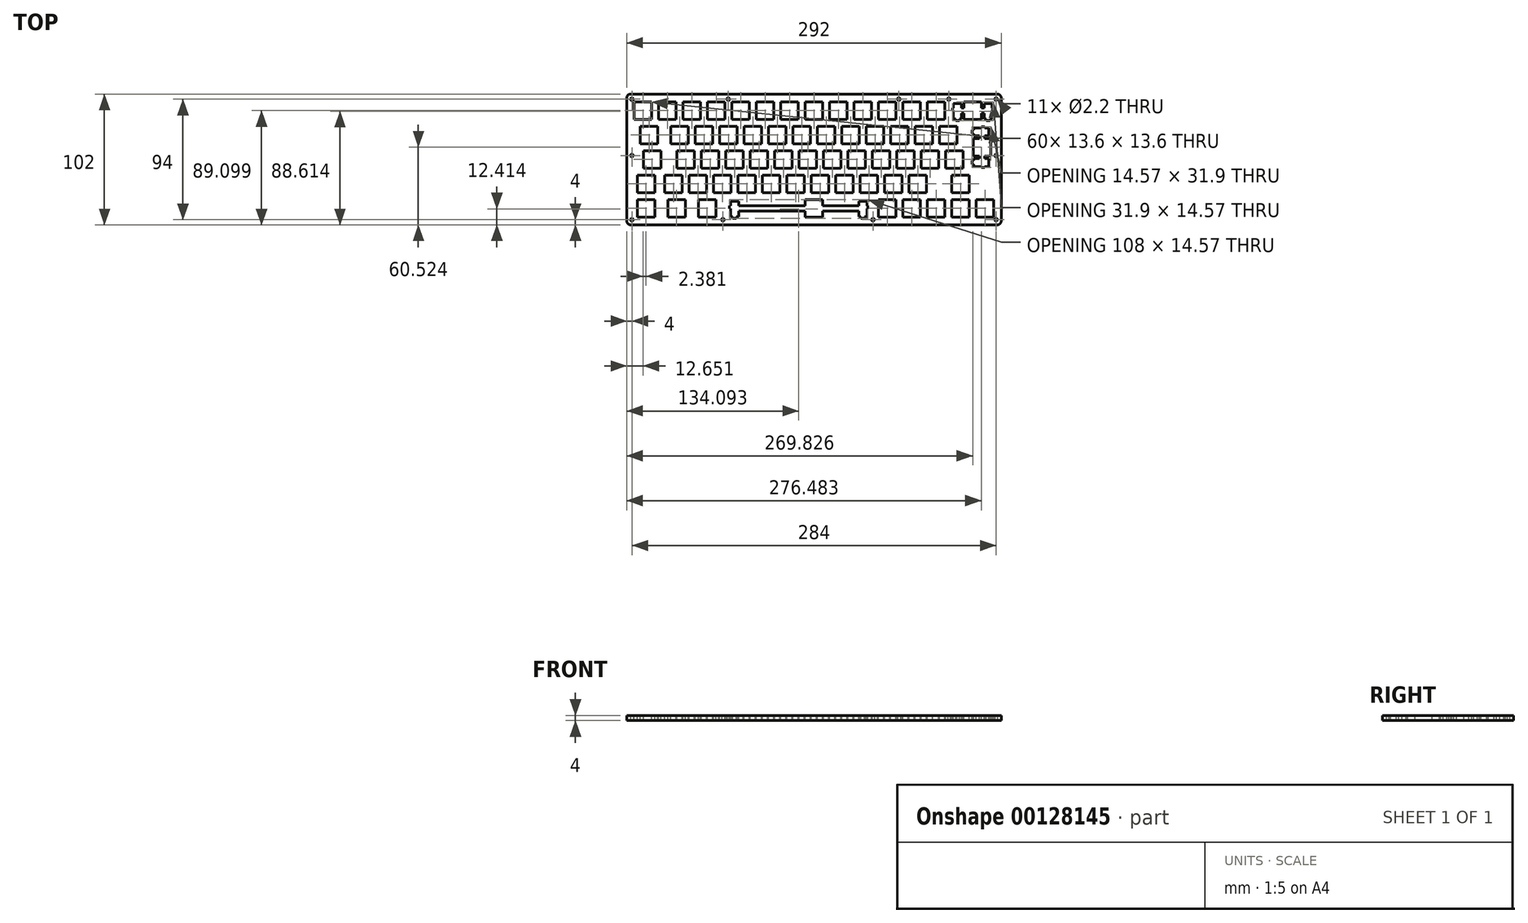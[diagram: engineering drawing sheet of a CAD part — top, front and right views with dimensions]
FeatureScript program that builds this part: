
annotation { "Feature Type Name" : "Feature", "Feature Type Description" : "" }
export const myFeature = defineFeature(function(context is Context, id is Id, definition is map)
    precondition{}
    {
        {
            var Q0;
            Q0=qCreatedBy(makeId("Top.planeOp"),FACE);
            var sketch = newSketch(context, id + "F0", { "sketchPlane" : qUnion([Q0])});
            skLineSegment(sketch, "E0.bottom", {"start": v(-143, 51) * mm, "end": v(143, 51) * mm});
            skLineSegment(sketch, "E0.top", {"start": v(-143, -51) * mm, "end": v(143, -51) * mm});
            skLineSegment(sketch, "E0.left", {"start": v(-146, 48) * mm, "end": v(-146, -48) * mm});
            skLineSegment(sketch, "E0.right", {"start": v(146, 48) * mm, "end": v(146, -48) * mm});
            skPoint(sketch, "E0.middle", {"position": v(0, 0) * mm});
            skPoint(sketch, "E1.visualSharp", {"position": v(-146, 51) * mm});
            skArc(sketch, "E1.filletArc", {"start": v(-143, 51) * mm, "mid": v(-145.12, 50.12) * mm, "end": v(-146, 48) * mm});
            skPoint(sketch, "E2.visualSharp", {"position": v(-146, -51) * mm});
            skArc(sketch, "E2.filletArc", {"start": v(-146, -48) * mm, "mid": v(-145.12, -50.12) * mm, "end": v(-143, -51) * mm});
            skPoint(sketch, "E3.visualSharp", {"position": v(146, 51) * mm});
            skArc(sketch, "E3.filletArc", {"start": v(146, 48) * mm, "mid": v(145.12, 50.12) * mm, "end": v(143, 51) * mm});
            skPoint(sketch, "E4.visualSharp", {"position": v(146, -51) * mm});
            skArc(sketch, "E4.filletArc", {"start": v(143, -51) * mm, "mid": v(145.12, -50.12) * mm, "end": v(146, -48) * mm});
            skCircle(sketch, "E5", {"center": v(-142, 47) * mm, "radius": 1.1 * mm});
            skCircle(sketch, "E6", {"center": v(-66.83, 47) * mm, "radius": 1.1 * mm});
            skCircle(sketch, "E7", {"center": v(66.17, 47) * mm, "radius": 1.1 * mm});
            skCircle(sketch, "E8", {"center": v(105.17, 47) * mm, "radius": 1.1 * mm});
            skCircle(sketch, "E9", {"center": v(142, 47) * mm, "radius": 1.1 * mm});
            skCircle(sketch, "E10", {"center": v(-142, -47) * mm, "radius": 1.1 * mm});
            skCircle(sketch, "E11", {"center": v(142, -47) * mm, "radius": 1.1 * mm});
            skCircle(sketch, "E12", {"center": v(-71, -47) * mm, "radius": 1.1 * mm});
            skCircle(sketch, "E13", {"center": v(46, -47) * mm, "radius": 1.1 * mm});
            skCircle(sketch, "E14", {"center": v(-142, 3) * mm, "radius": 1.1 * mm});
            skCircle(sketch, "E15", {"center": v(142, 3) * mm, "radius": 1.1 * mm});
            skSolve(sketch);
        }
        {
            var Q0;
            Q0 = qSketchRegion(id + "F0", true);
            extrude(context, id + "F1", {"entities" : qUnion([Q0]), "depth" : 4 * mm});
        }
        {
            var Q0;
            Q0=makeQuery(id+"F1.opExtrude","CAP_FACE",FACE,{"disambiguationData":[OSD([sQuery(id+"F0.wireOp",EDGE,"E0.bottom"),sQuery(id+"F0.wireOp",EDGE,"E0.top"),sQuery(id+"F0.wireOp",EDGE,"E0.left"),sQuery(id+"F0.wireOp",EDGE,"E0.right"),sQuery(id+"F0.wireOp",EDGE,"E1.filletArc"),sQuery(id+"F0.wireOp",EDGE,"E2.filletArc"),sQuery(id+"F0.wireOp",EDGE,"E3.filletArc"),sQuery(id+"F0.wireOp",EDGE,"E4.filletArc"),sQuery(id+"F0.wireOp",EDGE,"E5"),sQuery(id+"F0.wireOp",EDGE,"E6"),sQuery(id+"F0.wireOp",EDGE,"E7"),sQuery(id+"F0.wireOp",EDGE,"E8"),sQuery(id+"F0.wireOp",EDGE,"E9"),sQuery(id+"F0.wireOp",EDGE,"E10"),sQuery(id+"F0.wireOp",EDGE,"E11"),sQuery(id+"F0.wireOp",EDGE,"E12"),sQuery(id+"F0.wireOp",EDGE,"E13"),sQuery(id+"F0.wireOp",EDGE,"E14"),sQuery(id+"F0.wireOp",EDGE,"E15")])],"isStart":false});
            var sketch = newSketch(context, id + "F2", { "sketchPlane" : qUnion([Q0])});
            skLineSegment(sketch, "E16", {"start": v(-58.78, -36) * mm, "end": v(-58.78, -32.77) * mm});
            skLineSegment(sketch, "E17", {"start": v(-58.78, -32.77) * mm, "end": v(-65.03, -32.77) * mm});
            skLineSegment(sketch, "E18", {"start": v(-65.03, -32.77) * mm, "end": v(-65.03, -36) * mm});
            skLineSegment(sketch, "E19", {"start": v(-65.03, -36) * mm, "end": v(-65.9, -36) * mm});
            skLineSegment(sketch, "E20", {"start": v(-65.9, -36) * mm, "end": v(-65.9, -38.4) * mm});
            skLineSegment(sketch, "E21", {"start": v(-65.9, -38.4) * mm, "end": v(-65.03, -38.4) * mm});
            skLineSegment(sketch, "E22", {"start": v(-65.03, -38.4) * mm, "end": v(-65.03, -44.67) * mm});
            skLineSegment(sketch, "E23", {"start": v(-65.03, -44.67) * mm, "end": v(-63.36, -44.67) * mm});
            skLineSegment(sketch, "E24", {"start": v(-63.36, -44.67) * mm, "end": v(-63.36, -45.87) * mm});
            skLineSegment(sketch, "E25", {"start": v(-63.36, -45.87) * mm, "end": v(-60.46, -45.87) * mm});
            skLineSegment(sketch, "E26", {"start": v(-60.46, -45.87) * mm, "end": v(-60.46, -44.67) * mm});
            skLineSegment(sketch, "E27", {"start": v(-60.46, -44.67) * mm, "end": v(-58.78, -44.67) * mm});
            skLineSegment(sketch, "E28", {"start": v(-58.78, -44.67) * mm, "end": v(-58.78, -40.2) * mm});
            skLineSegment(sketch, "E29", {"start": v(-6.8, -44.9) * mm, "end": v(-6.8, -40.2) * mm});
            skLineSegment(sketch, "E30", {"start": v(6.8, -40.2) * mm, "end": v(34.97, -40.2) * mm});
            skLineSegment(sketch, "E31", {"start": v(34.97, -40.2) * mm, "end": v(34.97, -44.67) * mm});
            skLineSegment(sketch, "E32", {"start": v(34.97, -44.67) * mm, "end": v(36.64, -44.67) * mm});
            skLineSegment(sketch, "E33", {"start": v(36.64, -44.67) * mm, "end": v(36.64, -45.87) * mm});
            skLineSegment(sketch, "E34", {"start": v(36.64, -45.87) * mm, "end": v(39.54, -45.87) * mm});
            skLineSegment(sketch, "E35", {"start": v(39.54, -45.87) * mm, "end": v(39.54, -44.67) * mm});
            skLineSegment(sketch, "E36", {"start": v(39.54, -44.67) * mm, "end": v(41.22, -44.67) * mm});
            skLineSegment(sketch, "E37", {"start": v(41.22, -44.67) * mm, "end": v(41.22, -38.4) * mm});
            skLineSegment(sketch, "E38", {"start": v(41.22, -38.4) * mm, "end": v(42.1, -38.4) * mm});
            skLineSegment(sketch, "E39", {"start": v(42.1, -38.4) * mm, "end": v(42.1, -36) * mm});
            skLineSegment(sketch, "E40", {"start": v(42.1, -36) * mm, "end": v(41.22, -36) * mm});
            skLineSegment(sketch, "E41", {"start": v(41.22, -36) * mm, "end": v(41.22, -32.77) * mm});
            skLineSegment(sketch, "E42", {"start": v(41.22, -32.77) * mm, "end": v(34.97, -32.77) * mm});
            skLineSegment(sketch, "E43", {"start": v(34.97, -32.77) * mm, "end": v(34.97, -36) * mm});
            skLineSegment(sketch, "E44", {"start": v(34.97, -36) * mm, "end": v(6.8, -36) * mm});
            skLineSegment(sketch, "E45", {"start": v(-137.77, -31.3) * mm, "end": v(-124.17, -31.3) * mm});
            skLineSegment(sketch, "E46", {"start": v(-124.17, -31.3) * mm, "end": v(-124.17, -44.9) * mm});
            skLineSegment(sketch, "E47", {"start": v(-124.17, -44.9) * mm, "end": v(-137.77, -44.9) * mm});
            skLineSegment(sketch, "E48", {"start": v(-137.77, -44.9) * mm, "end": v(-137.77, -31.3) * mm});
            skLineSegment(sketch, "E49", {"start": v(-113.96, -31.3) * mm, "end": v(-100.36, -31.3) * mm});
            skLineSegment(sketch, "E50", {"start": v(-100.36, -31.3) * mm, "end": v(-100.36, -44.9) * mm});
            skLineSegment(sketch, "E51", {"start": v(-100.36, -44.9) * mm, "end": v(-113.96, -44.9) * mm});
            skLineSegment(sketch, "E52", {"start": v(-113.96, -44.9) * mm, "end": v(-113.96, -31.3) * mm});
            skLineSegment(sketch, "E53", {"start": v(-90.14, -31.3) * mm, "end": v(-76.54, -31.3) * mm});
            skLineSegment(sketch, "E54", {"start": v(-76.54, -31.3) * mm, "end": v(-76.54, -44.9) * mm});
            skLineSegment(sketch, "E55", {"start": v(-76.54, -44.9) * mm, "end": v(-90.14, -44.9) * mm});
            skLineSegment(sketch, "E56", {"start": v(-90.14, -44.9) * mm, "end": v(-90.14, -31.3) * mm});
            skLineSegment(sketch, "E57", {"start": v(50.35, -31.3) * mm, "end": v(63.95, -31.3) * mm});
            skLineSegment(sketch, "E58", {"start": v(63.95, -31.3) * mm, "end": v(63.95, -44.9) * mm});
            skLineSegment(sketch, "E59", {"start": v(63.95, -44.9) * mm, "end": v(50.35, -44.9) * mm});
            skLineSegment(sketch, "E60", {"start": v(50.35, -44.9) * mm, "end": v(50.35, -31.3) * mm});
            skLineSegment(sketch, "E61", {"start": v(69.4, -31.3) * mm, "end": v(83, -31.3) * mm});
            skLineSegment(sketch, "E62", {"start": v(83, -31.3) * mm, "end": v(83, -44.9) * mm});
            skLineSegment(sketch, "E63", {"start": v(83, -44.9) * mm, "end": v(69.4, -44.9) * mm});
            skLineSegment(sketch, "E64", {"start": v(69.4, -44.9) * mm, "end": v(69.4, -31.3) * mm});
            skLineSegment(sketch, "E65", {"start": v(88.45, -31.3) * mm, "end": v(102.05, -31.3) * mm});
            skLineSegment(sketch, "E66", {"start": v(102.05, -31.3) * mm, "end": v(102.05, -44.9) * mm});
            skLineSegment(sketch, "E67", {"start": v(102.05, -44.9) * mm, "end": v(88.45, -44.9) * mm});
            skLineSegment(sketch, "E68", {"start": v(88.45, -44.9) * mm, "end": v(88.45, -31.3) * mm});
            skLineSegment(sketch, "E69", {"start": v(107.5, -31.3) * mm, "end": v(121.1, -31.3) * mm});
            skLineSegment(sketch, "E70", {"start": v(121.1, -31.3) * mm, "end": v(121.1, -44.9) * mm});
            skLineSegment(sketch, "E71", {"start": v(121.1, -44.9) * mm, "end": v(107.5, -44.9) * mm});
            skLineSegment(sketch, "E72", {"start": v(107.5, -44.9) * mm, "end": v(107.5, -31.3) * mm});
            skLineSegment(sketch, "E73", {"start": v(126.55, -31.3) * mm, "end": v(140.15, -31.3) * mm});
            skLineSegment(sketch, "E74", {"start": v(140.15, -31.3) * mm, "end": v(140.15, -44.9) * mm});
            skLineSegment(sketch, "E75", {"start": v(140.15, -44.9) * mm, "end": v(126.55, -44.9) * mm});
            skLineSegment(sketch, "E76", {"start": v(126.55, -44.9) * mm, "end": v(126.55, -31.3) * mm});
            skLineSegment(sketch, "E77", {"start": v(-137.77, -12.25) * mm, "end": v(-124.17, -12.25) * mm});
            skLineSegment(sketch, "E78", {"start": v(-124.17, -12.25) * mm, "end": v(-124.17, -25.85) * mm});
            skLineSegment(sketch, "E79", {"start": v(-124.17, -25.85) * mm, "end": v(-137.77, -25.85) * mm});
            skLineSegment(sketch, "E80", {"start": v(-137.77, -25.85) * mm, "end": v(-137.77, -12.25) * mm});
            skLineSegment(sketch, "E81", {"start": v(-116.34, -12.25) * mm, "end": v(-102.74, -12.25) * mm});
            skLineSegment(sketch, "E82", {"start": v(-102.74, -12.25) * mm, "end": v(-102.74, -25.85) * mm});
            skLineSegment(sketch, "E83", {"start": v(-102.74, -25.85) * mm, "end": v(-116.34, -25.85) * mm});
            skLineSegment(sketch, "E84", {"start": v(-116.34, -25.85) * mm, "end": v(-116.34, -12.25) * mm});
            skLineSegment(sketch, "E85", {"start": v(-97.29, -12.25) * mm, "end": v(-83.69, -12.25) * mm});
            skLineSegment(sketch, "E86", {"start": v(-83.69, -12.25) * mm, "end": v(-83.69, -25.85) * mm});
            skLineSegment(sketch, "E87", {"start": v(-83.69, -25.85) * mm, "end": v(-97.29, -25.85) * mm});
            skLineSegment(sketch, "E88", {"start": v(-97.29, -25.85) * mm, "end": v(-97.29, -12.25) * mm});
            skLineSegment(sketch, "E89", {"start": v(-78.24, -12.25) * mm, "end": v(-64.64, -12.25) * mm});
            skLineSegment(sketch, "E90", {"start": v(-64.64, -12.25) * mm, "end": v(-64.64, -25.85) * mm});
            skLineSegment(sketch, "E91", {"start": v(-64.64, -25.85) * mm, "end": v(-78.24, -25.85) * mm});
            skLineSegment(sketch, "E92", {"start": v(-78.24, -25.85) * mm, "end": v(-78.24, -12.25) * mm});
            skLineSegment(sketch, "E93", {"start": v(-59.19, -12.25) * mm, "end": v(-45.59, -12.25) * mm});
            skLineSegment(sketch, "E94", {"start": v(-45.59, -12.25) * mm, "end": v(-45.59, -25.85) * mm});
            skLineSegment(sketch, "E95", {"start": v(-45.59, -25.85) * mm, "end": v(-59.19, -25.85) * mm});
            skLineSegment(sketch, "E96", {"start": v(-59.19, -25.85) * mm, "end": v(-59.19, -12.25) * mm});
            skLineSegment(sketch, "E97", {"start": v(-40.14, -12.25) * mm, "end": v(-26.54, -12.25) * mm});
            skLineSegment(sketch, "E98", {"start": v(-26.54, -12.25) * mm, "end": v(-26.54, -25.85) * mm});
            skLineSegment(sketch, "E99", {"start": v(-26.54, -25.85) * mm, "end": v(-40.14, -25.85) * mm});
            skLineSegment(sketch, "E100", {"start": v(-40.14, -25.85) * mm, "end": v(-40.14, -12.25) * mm});
            skLineSegment(sketch, "E101", {"start": v(-21.09, -12.25) * mm, "end": v(-7.49, -12.25) * mm});
            skLineSegment(sketch, "E102", {"start": v(-7.49, -12.25) * mm, "end": v(-7.49, -25.85) * mm});
            skLineSegment(sketch, "E103", {"start": v(-7.49, -25.85) * mm, "end": v(-21.09, -25.85) * mm});
            skLineSegment(sketch, "E104", {"start": v(-21.09, -25.85) * mm, "end": v(-21.09, -12.25) * mm});
            skLineSegment(sketch, "E105", {"start": v(-2.04, -12.25) * mm, "end": v(11.56, -12.25) * mm});
            skLineSegment(sketch, "E106", {"start": v(11.56, -12.25) * mm, "end": v(11.56, -25.85) * mm});
            skLineSegment(sketch, "E107", {"start": v(11.56, -25.85) * mm, "end": v(-2.04, -25.85) * mm});
            skLineSegment(sketch, "E108", {"start": v(-2.04, -25.85) * mm, "end": v(-2.04, -12.25) * mm});
            skLineSegment(sketch, "E109", {"start": v(17.01, -12.25) * mm, "end": v(30.61, -12.25) * mm});
            skLineSegment(sketch, "E110", {"start": v(30.61, -12.25) * mm, "end": v(30.61, -25.85) * mm});
            skLineSegment(sketch, "E111", {"start": v(30.61, -25.85) * mm, "end": v(17.01, -25.85) * mm});
            skLineSegment(sketch, "E112", {"start": v(17.01, -25.85) * mm, "end": v(17.01, -12.25) * mm});
            skLineSegment(sketch, "E113", {"start": v(36.06, -12.25) * mm, "end": v(49.66, -12.25) * mm});
            skLineSegment(sketch, "E114", {"start": v(49.66, -12.25) * mm, "end": v(49.66, -25.85) * mm});
            skLineSegment(sketch, "E115", {"start": v(49.66, -25.85) * mm, "end": v(36.06, -25.85) * mm});
            skLineSegment(sketch, "E116", {"start": v(36.06, -25.85) * mm, "end": v(36.06, -12.25) * mm});
            skLineSegment(sketch, "E117", {"start": v(55.11, -12.25) * mm, "end": v(68.71, -12.25) * mm});
            skLineSegment(sketch, "E118", {"start": v(68.71, -12.25) * mm, "end": v(68.71, -25.85) * mm});
            skLineSegment(sketch, "E119", {"start": v(68.71, -25.85) * mm, "end": v(55.11, -25.85) * mm});
            skLineSegment(sketch, "E120", {"start": v(55.11, -25.85) * mm, "end": v(55.11, -12.25) * mm});
            skLineSegment(sketch, "E121", {"start": v(74.16, -12.25) * mm, "end": v(87.76, -12.25) * mm});
            skLineSegment(sketch, "E122", {"start": v(87.76, -12.25) * mm, "end": v(87.76, -25.85) * mm});
            skLineSegment(sketch, "E123", {"start": v(87.76, -25.85) * mm, "end": v(74.16, -25.85) * mm});
            skLineSegment(sketch, "E124", {"start": v(74.16, -25.85) * mm, "end": v(74.16, -12.25) * mm});
            skLineSegment(sketch, "E125", {"start": v(107.5, -12.25) * mm, "end": v(121.1, -12.25) * mm});
            skLineSegment(sketch, "E126", {"start": v(121.1, -12.25) * mm, "end": v(121.1, -25.85) * mm});
            skLineSegment(sketch, "E127", {"start": v(121.1, -25.85) * mm, "end": v(107.5, -25.85) * mm});
            skLineSegment(sketch, "E128", {"start": v(107.5, -25.85) * mm, "end": v(107.5, -12.25) * mm});
            skLineSegment(sketch, "E129", {"start": v(-133, 6.8) * mm, "end": v(-119.4, 6.8) * mm});
            skLineSegment(sketch, "E130", {"start": v(-119.4, 6.8) * mm, "end": v(-119.4, -6.8) * mm});
            skLineSegment(sketch, "E131", {"start": v(-119.4, -6.8) * mm, "end": v(-133, -6.8) * mm});
            skLineSegment(sketch, "E132", {"start": v(-133, -6.8) * mm, "end": v(-133, 6.8) * mm});
            skLineSegment(sketch, "E133", {"start": v(-106.81, 6.8) * mm, "end": v(-93.21, 6.8) * mm});
            skLineSegment(sketch, "E134", {"start": v(-93.21, 6.8) * mm, "end": v(-93.21, -6.8) * mm});
            skLineSegment(sketch, "E135", {"start": v(-93.21, -6.8) * mm, "end": v(-106.81, -6.8) * mm});
            skLineSegment(sketch, "E136", {"start": v(-106.81, -6.8) * mm, "end": v(-106.81, 6.8) * mm});
            skLineSegment(sketch, "E137", {"start": v(-87.76, 6.8) * mm, "end": v(-74.16, 6.8) * mm});
            skLineSegment(sketch, "E138", {"start": v(-74.16, 6.8) * mm, "end": v(-74.16, -6.8) * mm});
            skLineSegment(sketch, "E139", {"start": v(-74.16, -6.8) * mm, "end": v(-87.76, -6.8) * mm});
            skLineSegment(sketch, "E140", {"start": v(-87.76, -6.8) * mm, "end": v(-87.76, 6.8) * mm});
            skLineSegment(sketch, "E141", {"start": v(-68.71, 6.8) * mm, "end": v(-55.11, 6.8) * mm});
            skLineSegment(sketch, "E142", {"start": v(-55.11, 6.8) * mm, "end": v(-55.11, -6.8) * mm});
            skLineSegment(sketch, "E143", {"start": v(-55.11, -6.8) * mm, "end": v(-68.71, -6.8) * mm});
            skLineSegment(sketch, "E144", {"start": v(-68.71, -6.8) * mm, "end": v(-68.71, 6.8) * mm});
            skLineSegment(sketch, "E145", {"start": v(-49.66, 6.8) * mm, "end": v(-36.06, 6.8) * mm});
            skLineSegment(sketch, "E146", {"start": v(-36.06, 6.8) * mm, "end": v(-36.06, -6.8) * mm});
            skLineSegment(sketch, "E147", {"start": v(-36.06, -6.8) * mm, "end": v(-49.66, -6.8) * mm});
            skLineSegment(sketch, "E148", {"start": v(-49.66, -6.8) * mm, "end": v(-49.66, 6.8) * mm});
            skLineSegment(sketch, "E149", {"start": v(-30.61, 6.8) * mm, "end": v(-17.01, 6.8) * mm});
            skLineSegment(sketch, "E150", {"start": v(-17.01, 6.8) * mm, "end": v(-17.01, -6.8) * mm});
            skLineSegment(sketch, "E151", {"start": v(-17.01, -6.8) * mm, "end": v(-30.61, -6.8) * mm});
            skLineSegment(sketch, "E152", {"start": v(-30.61, -6.8) * mm, "end": v(-30.61, 6.8) * mm});
            skLineSegment(sketch, "E153", {"start": v(-11.56, 6.8) * mm, "end": v(2.04, 6.8) * mm});
            skLineSegment(sketch, "E154", {"start": v(2.04, 6.8) * mm, "end": v(2.04, -6.8) * mm});
            skLineSegment(sketch, "E155", {"start": v(2.04, -6.8) * mm, "end": v(-11.56, -6.8) * mm});
            skLineSegment(sketch, "E156", {"start": v(-11.56, -6.8) * mm, "end": v(-11.56, 6.8) * mm});
            skLineSegment(sketch, "E157", {"start": v(7.49, 6.8) * mm, "end": v(21.09, 6.8) * mm});
            skLineSegment(sketch, "E158", {"start": v(21.09, 6.8) * mm, "end": v(21.09, -6.8) * mm});
            skLineSegment(sketch, "E159", {"start": v(21.09, -6.8) * mm, "end": v(7.49, -6.8) * mm});
            skLineSegment(sketch, "E160", {"start": v(7.49, -6.8) * mm, "end": v(7.49, 6.8) * mm});
            skLineSegment(sketch, "E161", {"start": v(26.54, 6.8) * mm, "end": v(40.14, 6.8) * mm});
            skLineSegment(sketch, "E162", {"start": v(40.14, 6.8) * mm, "end": v(40.14, -6.8) * mm});
            skLineSegment(sketch, "E163", {"start": v(40.14, -6.8) * mm, "end": v(26.54, -6.8) * mm});
            skLineSegment(sketch, "E164", {"start": v(26.54, -6.8) * mm, "end": v(26.54, 6.8) * mm});
            skLineSegment(sketch, "E165", {"start": v(45.59, 6.8) * mm, "end": v(59.19, 6.8) * mm});
            skLineSegment(sketch, "E166", {"start": v(59.19, 6.8) * mm, "end": v(59.19, -6.8) * mm});
            skLineSegment(sketch, "E167", {"start": v(59.19, -6.8) * mm, "end": v(45.59, -6.8) * mm});
            skLineSegment(sketch, "E168", {"start": v(45.59, -6.8) * mm, "end": v(45.59, 6.8) * mm});
            skLineSegment(sketch, "E169", {"start": v(64.64, 6.8) * mm, "end": v(78.24, 6.8) * mm});
            skLineSegment(sketch, "E170", {"start": v(78.24, 6.8) * mm, "end": v(78.24, -6.8) * mm});
            skLineSegment(sketch, "E171", {"start": v(78.24, -6.8) * mm, "end": v(64.64, -6.8) * mm});
            skLineSegment(sketch, "E172", {"start": v(64.64, -6.8) * mm, "end": v(64.64, 6.8) * mm});
            skLineSegment(sketch, "E173", {"start": v(83.69, 6.8) * mm, "end": v(97.29, 6.8) * mm});
            skLineSegment(sketch, "E174", {"start": v(97.29, 6.8) * mm, "end": v(97.29, -6.8) * mm});
            skLineSegment(sketch, "E175", {"start": v(97.29, -6.8) * mm, "end": v(83.69, -6.8) * mm});
            skLineSegment(sketch, "E176", {"start": v(83.69, -6.8) * mm, "end": v(83.69, 6.8) * mm});
            skLineSegment(sketch, "E177", {"start": v(102.74, 6.8) * mm, "end": v(116.34, 6.8) * mm});
            skLineSegment(sketch, "E178", {"start": v(116.34, 6.8) * mm, "end": v(116.34, -6.8) * mm});
            skLineSegment(sketch, "E179", {"start": v(116.34, -6.8) * mm, "end": v(102.74, -6.8) * mm});
            skLineSegment(sketch, "E180", {"start": v(102.74, -6.8) * mm, "end": v(102.74, 6.8) * mm});
            skLineSegment(sketch, "E181", {"start": v(130.67, 25.47) * mm, "end": v(130.67, 24.6) * mm});
            skLineSegment(sketch, "E182", {"start": v(130.67, 24.6) * mm, "end": v(124.4, 24.6) * mm});
            skLineSegment(sketch, "E183", {"start": v(124.4, 24.6) * mm, "end": v(124.4, 22.93) * mm});
            skLineSegment(sketch, "E184", {"start": v(124.4, 22.93) * mm, "end": v(123.2, 22.93) * mm});
            skLineSegment(sketch, "E185", {"start": v(123.2, 22.93) * mm, "end": v(123.2, 20.02) * mm});
            skLineSegment(sketch, "E186", {"start": v(123.2, 20.02) * mm, "end": v(124.4, 20.02) * mm});
            skLineSegment(sketch, "E187", {"start": v(124.4, 20.02) * mm, "end": v(124.4, 18.35) * mm});
            skLineSegment(sketch, "E188", {"start": v(124.4, 18.35) * mm, "end": v(128.87, 18.35) * mm});
            skLineSegment(sketch, "E189", {"start": v(128.87, 18.35) * mm, "end": v(128.87, 16.32) * mm});
            skLineSegment(sketch, "E190", {"start": v(128.87, 16.32) * mm, "end": v(124.17, 16.32) * mm});
            skLineSegment(sketch, "E191", {"start": v(124.17, 16.32) * mm, "end": v(124.17, 2.72) * mm});
            skLineSegment(sketch, "E192", {"start": v(124.17, 2.72) * mm, "end": v(128.87, 2.72) * mm});
            skLineSegment(sketch, "E193", {"start": v(128.87, 2.72) * mm, "end": v(128.87, 0.7) * mm});
            skLineSegment(sketch, "E194", {"start": v(128.87, 0.7) * mm, "end": v(124.4, 0.7) * mm});
            skLineSegment(sketch, "E195", {"start": v(124.4, 0.7) * mm, "end": v(124.4, -0.98) * mm});
            skLineSegment(sketch, "E196", {"start": v(124.4, -0.98) * mm, "end": v(123.2, -0.98) * mm});
            skLineSegment(sketch, "E197", {"start": v(123.2, -0.98) * mm, "end": v(123.2, -3.88) * mm});
            skLineSegment(sketch, "E198", {"start": v(123.2, -3.88) * mm, "end": v(124.4, -3.88) * mm});
            skLineSegment(sketch, "E199", {"start": v(124.4, -3.88) * mm, "end": v(124.4, -5.55) * mm});
            skLineSegment(sketch, "E200", {"start": v(124.4, -5.55) * mm, "end": v(130.67, -5.55) * mm});
            skLineSegment(sketch, "E201", {"start": v(130.67, -5.55) * mm, "end": v(130.67, -6.43) * mm});
            skLineSegment(sketch, "E202", {"start": v(130.67, -6.43) * mm, "end": v(133.07, -6.43) * mm});
            skLineSegment(sketch, "E203", {"start": v(133.07, -6.43) * mm, "end": v(133.07, -5.55) * mm});
            skLineSegment(sketch, "E204", {"start": v(133.07, -5.55) * mm, "end": v(136.3, -5.55) * mm});
            skLineSegment(sketch, "E205", {"start": v(136.3, -5.55) * mm, "end": v(136.3, 0.7) * mm});
            skLineSegment(sketch, "E206", {"start": v(136.3, 0.7) * mm, "end": v(133.07, 0.7) * mm});
            skLineSegment(sketch, "E207", {"start": v(133.07, 0.7) * mm, "end": v(133.07, 2.72) * mm});
            skLineSegment(sketch, "E208", {"start": v(133.07, 2.72) * mm, "end": v(137.77, 2.72) * mm});
            skLineSegment(sketch, "E209", {"start": v(137.77, 2.72) * mm, "end": v(137.77, 16.32) * mm});
            skLineSegment(sketch, "E210", {"start": v(137.77, 16.32) * mm, "end": v(133.07, 16.32) * mm});
            skLineSegment(sketch, "E211", {"start": v(133.07, 16.32) * mm, "end": v(133.07, 18.35) * mm});
            skLineSegment(sketch, "E212", {"start": v(133.07, 18.35) * mm, "end": v(136.3, 18.35) * mm});
            skLineSegment(sketch, "E213", {"start": v(136.3, 18.35) * mm, "end": v(136.3, 24.6) * mm});
            skLineSegment(sketch, "E214", {"start": v(136.3, 24.6) * mm, "end": v(133.07, 24.6) * mm});
            skLineSegment(sketch, "E215", {"start": v(133.07, 24.6) * mm, "end": v(133.07, 25.47) * mm});
            skLineSegment(sketch, "E216", {"start": v(133.07, 25.47) * mm, "end": v(130.67, 25.47) * mm});
            skLineSegment(sketch, "E217", {"start": v(-135.39, 25.85) * mm, "end": v(-121.79, 25.85) * mm});
            skLineSegment(sketch, "E218", {"start": v(-121.79, 25.85) * mm, "end": v(-121.79, 12.25) * mm});
            skLineSegment(sketch, "E219", {"start": v(-121.79, 12.25) * mm, "end": v(-135.39, 12.25) * mm});
            skLineSegment(sketch, "E220", {"start": v(-135.39, 12.25) * mm, "end": v(-135.39, 25.85) * mm});
            skLineSegment(sketch, "E221", {"start": v(-111.57, 25.85) * mm, "end": v(-97.98, 25.85) * mm});
            skLineSegment(sketch, "E222", {"start": v(-97.98, 25.85) * mm, "end": v(-97.98, 12.25) * mm});
            skLineSegment(sketch, "E223", {"start": v(-97.98, 12.25) * mm, "end": v(-111.57, 12.25) * mm});
            skLineSegment(sketch, "E224", {"start": v(-111.57, 12.25) * mm, "end": v(-111.57, 25.85) * mm});
            skLineSegment(sketch, "E225", {"start": v(-92.52, 25.85) * mm, "end": v(-78.93, 25.85) * mm});
            skLineSegment(sketch, "E226", {"start": v(-78.93, 25.85) * mm, "end": v(-78.93, 12.25) * mm});
            skLineSegment(sketch, "E227", {"start": v(-78.93, 12.25) * mm, "end": v(-92.52, 12.25) * mm});
            skLineSegment(sketch, "E228", {"start": v(-92.52, 12.25) * mm, "end": v(-92.52, 25.85) * mm});
            skLineSegment(sketch, "E229", {"start": v(-73.47, 25.85) * mm, "end": v(-59.88, 25.85) * mm});
            skLineSegment(sketch, "E230", {"start": v(-59.88, 25.85) * mm, "end": v(-59.88, 12.25) * mm});
            skLineSegment(sketch, "E231", {"start": v(-59.88, 12.25) * mm, "end": v(-73.47, 12.25) * mm});
            skLineSegment(sketch, "E232", {"start": v(-73.47, 12.25) * mm, "end": v(-73.47, 25.85) * mm});
            skLineSegment(sketch, "E233", {"start": v(-54.43, 25.85) * mm, "end": v(-40.83, 25.85) * mm});
            skLineSegment(sketch, "E234", {"start": v(-40.83, 25.85) * mm, "end": v(-40.83, 12.25) * mm});
            skLineSegment(sketch, "E235", {"start": v(-40.83, 12.25) * mm, "end": v(-54.43, 12.25) * mm});
            skLineSegment(sketch, "E236", {"start": v(-54.43, 12.25) * mm, "end": v(-54.43, 25.85) * mm});
            skLineSegment(sketch, "E237", {"start": v(-35.38, 25.85) * mm, "end": v(-21.78, 25.85) * mm});
            skLineSegment(sketch, "E238", {"start": v(-21.78, 25.85) * mm, "end": v(-21.78, 12.25) * mm});
            skLineSegment(sketch, "E239", {"start": v(-21.78, 12.25) * mm, "end": v(-35.38, 12.25) * mm});
            skLineSegment(sketch, "E240", {"start": v(-35.38, 12.25) * mm, "end": v(-35.38, 25.85) * mm});
            skLineSegment(sketch, "E241", {"start": v(-16.33, 25.85) * mm, "end": v(-2.72, 25.85) * mm});
            skLineSegment(sketch, "E242", {"start": v(-2.72, 25.85) * mm, "end": v(-2.72, 12.25) * mm});
            skLineSegment(sketch, "E243", {"start": v(-2.72, 12.25) * mm, "end": v(-16.33, 12.25) * mm});
            skLineSegment(sketch, "E244", {"start": v(-16.33, 12.25) * mm, "end": v(-16.33, 25.85) * mm});
            skLineSegment(sketch, "E245", {"start": v(2.72, 25.85) * mm, "end": v(16.33, 25.85) * mm});
            skLineSegment(sketch, "E246", {"start": v(16.33, 25.85) * mm, "end": v(16.33, 12.25) * mm});
            skLineSegment(sketch, "E247", {"start": v(16.33, 12.25) * mm, "end": v(2.72, 12.25) * mm});
            skLineSegment(sketch, "E248", {"start": v(2.72, 12.25) * mm, "end": v(2.72, 25.85) * mm});
            skLineSegment(sketch, "E249", {"start": v(21.78, 25.85) * mm, "end": v(35.38, 25.85) * mm});
            skLineSegment(sketch, "E250", {"start": v(35.38, 25.85) * mm, "end": v(35.38, 12.25) * mm});
            skLineSegment(sketch, "E251", {"start": v(35.38, 12.25) * mm, "end": v(21.78, 12.25) * mm});
            skLineSegment(sketch, "E252", {"start": v(21.78, 12.25) * mm, "end": v(21.78, 25.85) * mm});
            skLineSegment(sketch, "E253", {"start": v(40.83, 25.85) * mm, "end": v(54.43, 25.85) * mm});
            skLineSegment(sketch, "E254", {"start": v(54.43, 25.85) * mm, "end": v(54.43, 12.25) * mm});
            skLineSegment(sketch, "E255", {"start": v(54.43, 12.25) * mm, "end": v(40.83, 12.25) * mm});
            skLineSegment(sketch, "E256", {"start": v(40.83, 12.25) * mm, "end": v(40.83, 25.85) * mm});
            skLineSegment(sketch, "E257", {"start": v(59.88, 25.85) * mm, "end": v(73.48, 25.85) * mm});
            skLineSegment(sketch, "E258", {"start": v(73.48, 25.85) * mm, "end": v(73.48, 12.25) * mm});
            skLineSegment(sketch, "E259", {"start": v(73.48, 12.25) * mm, "end": v(59.88, 12.25) * mm});
            skLineSegment(sketch, "E260", {"start": v(59.88, 12.25) * mm, "end": v(59.88, 25.85) * mm});
            skLineSegment(sketch, "E261", {"start": v(78.93, 25.85) * mm, "end": v(92.53, 25.85) * mm});
            skLineSegment(sketch, "E262", {"start": v(92.53, 25.85) * mm, "end": v(92.53, 12.25) * mm});
            skLineSegment(sketch, "E263", {"start": v(92.53, 12.25) * mm, "end": v(78.93, 12.25) * mm});
            skLineSegment(sketch, "E264", {"start": v(78.93, 12.25) * mm, "end": v(78.93, 25.85) * mm});
            skLineSegment(sketch, "E265", {"start": v(97.98, 25.85) * mm, "end": v(111.57, 25.85) * mm});
            skLineSegment(sketch, "E266", {"start": v(111.57, 25.85) * mm, "end": v(111.57, 12.25) * mm});
            skLineSegment(sketch, "E267", {"start": v(111.57, 12.25) * mm, "end": v(97.98, 12.25) * mm});
            skLineSegment(sketch, "E268", {"start": v(97.98, 12.25) * mm, "end": v(97.98, 25.85) * mm});
            skLineSegment(sketch, "E269", {"start": v(117.03, 44.9) * mm, "end": v(117.03, 40.2) * mm});
            skLineSegment(sketch, "E270", {"start": v(117.03, 40.2) * mm, "end": v(115, 40.2) * mm});
            skLineSegment(sketch, "E271", {"start": v(115, 40.2) * mm, "end": v(115, 43.43) * mm});
            skLineSegment(sketch, "E272", {"start": v(115, 43.43) * mm, "end": v(108.75, 43.43) * mm});
            skLineSegment(sketch, "E273", {"start": v(108.75, 43.43) * mm, "end": v(108.75, 40.2) * mm});
            skLineSegment(sketch, "E274", {"start": v(108.75, 40.2) * mm, "end": v(107.88, 40.2) * mm});
            skLineSegment(sketch, "E275", {"start": v(107.88, 40.2) * mm, "end": v(107.88, 37.8) * mm});
            skLineSegment(sketch, "E276", {"start": v(107.88, 37.8) * mm, "end": v(108.75, 37.8) * mm});
            skLineSegment(sketch, "E277", {"start": v(108.75, 37.8) * mm, "end": v(108.75, 31.53) * mm});
            skLineSegment(sketch, "E278", {"start": v(108.75, 31.53) * mm, "end": v(110.43, 31.53) * mm});
            skLineSegment(sketch, "E279", {"start": v(110.43, 31.53) * mm, "end": v(110.43, 30.33) * mm});
            skLineSegment(sketch, "E280", {"start": v(110.43, 30.33) * mm, "end": v(113.32, 30.33) * mm});
            skLineSegment(sketch, "E281", {"start": v(113.32, 30.33) * mm, "end": v(113.32, 31.53) * mm});
            skLineSegment(sketch, "E282", {"start": v(113.32, 31.53) * mm, "end": v(115, 31.53) * mm});
            skLineSegment(sketch, "E283", {"start": v(115, 31.53) * mm, "end": v(115, 36) * mm});
            skLineSegment(sketch, "E284", {"start": v(115, 36) * mm, "end": v(117.03, 36) * mm});
            skLineSegment(sketch, "E285", {"start": v(117.03, 36) * mm, "end": v(117.03, 31.3) * mm});
            skLineSegment(sketch, "E286", {"start": v(117.03, 31.3) * mm, "end": v(130.63, 31.3) * mm});
            skLineSegment(sketch, "E287", {"start": v(130.63, 31.3) * mm, "end": v(130.63, 36) * mm});
            skLineSegment(sketch, "E288", {"start": v(130.63, 36) * mm, "end": v(132.65, 36) * mm});
            skLineSegment(sketch, "E289", {"start": v(132.65, 36) * mm, "end": v(132.65, 31.53) * mm});
            skLineSegment(sketch, "E290", {"start": v(132.65, 31.53) * mm, "end": v(134.33, 31.53) * mm});
            skLineSegment(sketch, "E291", {"start": v(134.33, 31.53) * mm, "end": v(134.33, 30.33) * mm});
            skLineSegment(sketch, "E292", {"start": v(134.33, 30.33) * mm, "end": v(137.22, 30.33) * mm});
            skLineSegment(sketch, "E293", {"start": v(137.22, 30.33) * mm, "end": v(137.22, 31.53) * mm});
            skLineSegment(sketch, "E294", {"start": v(137.22, 31.53) * mm, "end": v(138.9, 31.53) * mm});
            skLineSegment(sketch, "E295", {"start": v(138.9, 31.53) * mm, "end": v(138.9, 37.8) * mm});
            skLineSegment(sketch, "E296", {"start": v(138.9, 37.8) * mm, "end": v(139.78, 37.8) * mm});
            skLineSegment(sketch, "E297", {"start": v(139.78, 37.8) * mm, "end": v(139.78, 40.2) * mm});
            skLineSegment(sketch, "E298", {"start": v(139.78, 40.2) * mm, "end": v(138.9, 40.2) * mm});
            skLineSegment(sketch, "E299", {"start": v(138.9, 40.2) * mm, "end": v(138.9, 43.43) * mm});
            skLineSegment(sketch, "E300", {"start": v(138.9, 43.43) * mm, "end": v(132.65, 43.43) * mm});
            skLineSegment(sketch, "E301", {"start": v(132.65, 43.43) * mm, "end": v(132.65, 40.2) * mm});
            skLineSegment(sketch, "E302", {"start": v(132.65, 40.2) * mm, "end": v(130.63, 40.2) * mm});
            skLineSegment(sketch, "E303", {"start": v(130.63, 40.2) * mm, "end": v(130.63, 44.9) * mm});
            skLineSegment(sketch, "E304", {"start": v(130.63, 44.9) * mm, "end": v(117.03, 44.9) * mm});
            skLineSegment(sketch, "E305", {"start": v(-140.15, 44.9) * mm, "end": v(-126.55, 44.9) * mm});
            skLineSegment(sketch, "E306", {"start": v(-126.55, 44.9) * mm, "end": v(-126.55, 31.3) * mm});
            skLineSegment(sketch, "E307", {"start": v(-126.55, 31.3) * mm, "end": v(-140.15, 31.3) * mm});
            skLineSegment(sketch, "E308", {"start": v(-140.15, 31.3) * mm, "end": v(-140.15, 44.9) * mm});
            skLineSegment(sketch, "E309", {"start": v(-121.1, 44.9) * mm, "end": v(-107.5, 44.9) * mm});
            skLineSegment(sketch, "E310", {"start": v(-107.5, 44.9) * mm, "end": v(-107.5, 31.3) * mm});
            skLineSegment(sketch, "E311", {"start": v(-107.5, 31.3) * mm, "end": v(-121.1, 31.3) * mm});
            skLineSegment(sketch, "E312", {"start": v(-121.1, 31.3) * mm, "end": v(-121.1, 44.9) * mm});
            skLineSegment(sketch, "E313", {"start": v(-102.05, 44.9) * mm, "end": v(-88.45, 44.9) * mm});
            skLineSegment(sketch, "E314", {"start": v(-88.45, 44.9) * mm, "end": v(-88.45, 31.3) * mm});
            skLineSegment(sketch, "E315", {"start": v(-88.45, 31.3) * mm, "end": v(-102.05, 31.3) * mm});
            skLineSegment(sketch, "E316", {"start": v(-102.05, 31.3) * mm, "end": v(-102.05, 44.9) * mm});
            skLineSegment(sketch, "E317", {"start": v(-83, 44.9) * mm, "end": v(-69.4, 44.9) * mm});
            skLineSegment(sketch, "E318", {"start": v(-69.4, 44.9) * mm, "end": v(-69.4, 31.3) * mm});
            skLineSegment(sketch, "E319", {"start": v(-69.4, 31.3) * mm, "end": v(-83, 31.3) * mm});
            skLineSegment(sketch, "E320", {"start": v(-83, 31.3) * mm, "end": v(-83, 44.9) * mm});
            skLineSegment(sketch, "E321", {"start": v(-63.95, 44.9) * mm, "end": v(-50.35, 44.9) * mm});
            skLineSegment(sketch, "E322", {"start": v(-50.35, 44.9) * mm, "end": v(-50.35, 31.3) * mm});
            skLineSegment(sketch, "E323", {"start": v(-50.35, 31.3) * mm, "end": v(-63.95, 31.3) * mm});
            skLineSegment(sketch, "E324", {"start": v(-63.95, 31.3) * mm, "end": v(-63.95, 44.9) * mm});
            skLineSegment(sketch, "E325", {"start": v(-44.9, 44.9) * mm, "end": v(-31.3, 44.9) * mm});
            skLineSegment(sketch, "E326", {"start": v(-31.3, 44.9) * mm, "end": v(-31.3, 31.3) * mm});
            skLineSegment(sketch, "E327", {"start": v(-31.3, 31.3) * mm, "end": v(-44.9, 31.3) * mm});
            skLineSegment(sketch, "E328", {"start": v(-44.9, 31.3) * mm, "end": v(-44.9, 44.9) * mm});
            skLineSegment(sketch, "E329", {"start": v(-25.85, 44.9) * mm, "end": v(-12.25, 44.9) * mm});
            skLineSegment(sketch, "E330", {"start": v(-12.25, 44.9) * mm, "end": v(-12.25, 31.3) * mm});
            skLineSegment(sketch, "E331", {"start": v(-12.25, 31.3) * mm, "end": v(-25.85, 31.3) * mm});
            skLineSegment(sketch, "E332", {"start": v(-25.85, 31.3) * mm, "end": v(-25.85, 44.9) * mm});
            skLineSegment(sketch, "E333", {"start": v(-6.8, 44.9) * mm, "end": v(6.8, 44.9) * mm});
            skLineSegment(sketch, "E334", {"start": v(6.8, 44.9) * mm, "end": v(6.8, 31.3) * mm});
            skLineSegment(sketch, "E335", {"start": v(6.8, 31.3) * mm, "end": v(-6.8, 31.3) * mm});
            skLineSegment(sketch, "E336", {"start": v(-6.8, 31.3) * mm, "end": v(-6.8, 44.9) * mm});
            skLineSegment(sketch, "E337", {"start": v(12.25, 44.9) * mm, "end": v(25.85, 44.9) * mm});
            skLineSegment(sketch, "E338", {"start": v(25.85, 44.9) * mm, "end": v(25.85, 31.3) * mm});
            skLineSegment(sketch, "E339", {"start": v(25.85, 31.3) * mm, "end": v(12.25, 31.3) * mm});
            skLineSegment(sketch, "E340", {"start": v(12.25, 31.3) * mm, "end": v(12.25, 44.9) * mm});
            skLineSegment(sketch, "E341", {"start": v(31.3, 44.9) * mm, "end": v(44.9, 44.9) * mm});
            skLineSegment(sketch, "E342", {"start": v(44.9, 44.9) * mm, "end": v(44.9, 31.3) * mm});
            skLineSegment(sketch, "E343", {"start": v(44.9, 31.3) * mm, "end": v(31.3, 31.3) * mm});
            skLineSegment(sketch, "E344", {"start": v(31.3, 31.3) * mm, "end": v(31.3, 44.9) * mm});
            skLineSegment(sketch, "E345", {"start": v(50.35, 44.9) * mm, "end": v(63.95, 44.9) * mm});
            skLineSegment(sketch, "E346", {"start": v(63.95, 44.9) * mm, "end": v(63.95, 31.3) * mm});
            skLineSegment(sketch, "E347", {"start": v(63.95, 31.3) * mm, "end": v(50.35, 31.3) * mm});
            skLineSegment(sketch, "E348", {"start": v(50.35, 31.3) * mm, "end": v(50.35, 44.9) * mm});
            skLineSegment(sketch, "E349", {"start": v(69.4, 44.9) * mm, "end": v(83, 44.9) * mm});
            skLineSegment(sketch, "E350", {"start": v(83, 44.9) * mm, "end": v(83, 31.3) * mm});
            skLineSegment(sketch, "E351", {"start": v(83, 31.3) * mm, "end": v(69.4, 31.3) * mm});
            skLineSegment(sketch, "E352", {"start": v(69.4, 31.3) * mm, "end": v(69.4, 44.9) * mm});
            skLineSegment(sketch, "E353", {"start": v(88.45, 44.9) * mm, "end": v(102.05, 44.9) * mm});
            skLineSegment(sketch, "E354", {"start": v(102.05, 44.9) * mm, "end": v(102.05, 31.3) * mm});
            skLineSegment(sketch, "E355", {"start": v(102.05, 31.3) * mm, "end": v(88.45, 31.3) * mm});
            skLineSegment(sketch, "E356", {"start": v(88.45, 31.3) * mm, "end": v(88.45, 44.9) * mm});
            skLineSegment(sketch, "E357.bottom", {"start": v(-6.8, -44.9) * mm, "end": v(6.8, -44.9) * mm});
            skLineSegment(sketch, "E357.top", {"start": v(-6.8, -31.3) * mm, "end": v(6.8, -31.3) * mm});
            skLineSegment(sketch, "E357.right", {"start": v(6.8, -44.9) * mm, "end": v(6.8, -40.2) * mm});
            skPoint(sketch, "E357.middle", {"position": v(0, -38.1) * mm});
            skPoint(sketch, "E357.middle.positionSnap0", {"position": v(50.35, -38.1) * mm});
            skPoint(sketch, "E357.centerSnap0", {"position": v(50.35, -38.1) * mm});
            skLineSegment(sketch, "E358", {"start": v(6.8, -31.3) * mm, "end": v(6.8, -36) * mm});
            skLineSegment(sketch, "E359", {"start": v(-6.8, -36) * mm, "end": v(-6.8, -31.3) * mm});
            skPoint(sketch, "E360.end.orphan", {"position": v(-6.8, -31.3) * mm});
            skLineSegment(sketch, "E361.trimOffspring", {"start": v(6.8, -40.2) * mm, "end": v(6.8, -44.9) * mm});
            skPoint(sketch, "E362.orphan", {"position": v(-6.8, -44.9) * mm});
            skLineSegment(sketch, "E363.trimOffspring", {"start": v(6.8, -36) * mm, "end": v(6.8, -31.3) * mm});
            skLineSegment(sketch, "E364", {"start": v(-58.78, -36) * mm, "end": v(-6.8, -36) * mm});
            skLineSegment(sketch, "E365", {"start": v(-58.78, -40.2) * mm, "end": v(-6.8, -40.2) * mm});
            skSolve(sketch);
        }
        {
            var Q0;
            Q0 = qSketchRegion(id + "F2", true);
            extrude(context, id + "F3", {"entities" : qUnion([Q0]), "operationType" : NewBodyOperationType.REMOVE, "endBound" : BoundingType.THROUGH_ALL, "oppositeDirection" : true, "depth" : 25 * mm});
        }
    });
